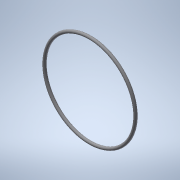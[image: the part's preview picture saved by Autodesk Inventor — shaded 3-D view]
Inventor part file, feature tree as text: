
AUTODESK INVENTOR PART (.ipt)
format: ipt  version: 2020.2 (Build 242310000, 310)  size: 116,224 bytes
history: native  units: mm
features: revolve x1, sketch x1
ambient origin geometry x8: Origin, YZ Plane, XZ Plane, XY Plane, X Axis, Y Axis, Z Axis, Center Point
bodies: Volumenkörper1 (feature_tree)
feature tree (2):
  revolve  "Umdrehung1"
  sketch  "Skizze1"  dims[d0=1.5mm d1=23.75mm d2=90.0deg]
